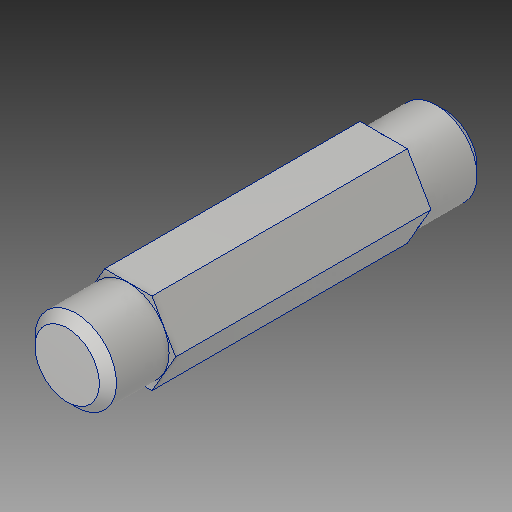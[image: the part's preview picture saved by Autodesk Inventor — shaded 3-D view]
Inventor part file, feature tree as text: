
AUTODESK INVENTOR PART (.ipt)
format: ipt  version: 2017 (Build 210142000, 142)  size: 105,984 bytes
history: native  units: in
note: dims shown in document units (in); Inventor stores cm internally (conversion verified against a paired STEP export)
features: chamfer x1
ambient origin geometry x8: Origin, YZ Plane, XZ Plane, XY Plane, X Axis, Y Axis, Z Axis, Center Point
bodies: Solid1 (feature_tree)
feature tree (1):
  chamfer  "Chamfer1"  [1 undecoded]
note: 1 required parameter value undecoded (feature->parameter linkage not recoverable at this tier; creation-order binding heuristic only, values carry confidence <= 0.55)
